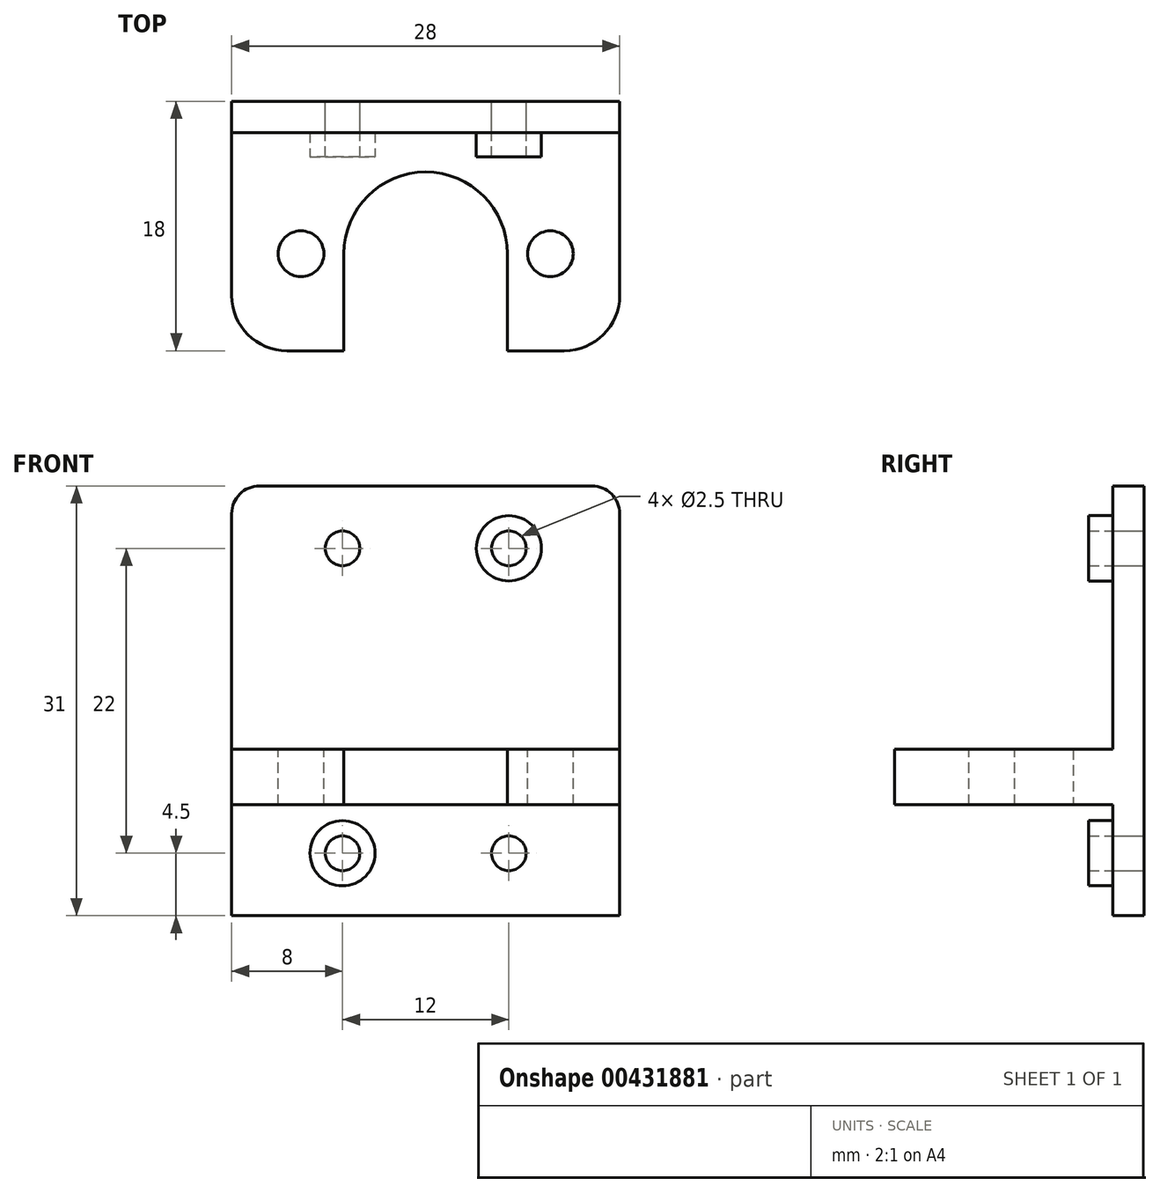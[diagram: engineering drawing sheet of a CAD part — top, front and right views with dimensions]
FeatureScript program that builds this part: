
annotation { "Feature Type Name" : "Feature", "Feature Type Description" : "" }
export const myFeature = defineFeature(function(context is Context, id is Id, definition is map)
    precondition{}
    {
        {
            var Q0;
            Q0=qCreatedBy(makeId("Front.planeOp"),FACE);
            var sketch = newSketch(context, id + "F0", { "sketchPlane" : qUnion([Q0])});
            skLineSegment(sketch, "E0.bottom", {"start": v(28, 31) * mm, "end": v(0, 31) * mm});
            skLineSegment(sketch, "E0.top", {"start": v(28, 0) * mm, "end": v(0, 0) * mm});
            skLineSegment(sketch, "E0.left", {"start": v(28, 31) * mm, "end": v(28, 0) * mm});
            skLineSegment(sketch, "E0.right", {"start": v(0, 31) * mm, "end": v(0, 0) * mm});
            skSolve(sketch);
        }
        {
            var Q0;
            Q0=makeQuery(id+"F0.imprint","IMPRINT",FACE,{"disambiguationData":[TD([[makeQuery(id+"F0.imprint","IMPRINT",EDGE,{"derivedFrom":sQuery(id+"F0.wireOp",EDGE,"E0.bottom")}),1.0]])]});
            extrude(context, id + "F1", {"entities" : qUnion([Q0]), "depth" : 4 * mm});
        }
        {
            var Q0;
            Q0=makeQuery(id+"F1.opExtrude","CAP_FACE",FACE,{"disambiguationData":[OSD([sQuery(id+"F0.wireOp",EDGE,"E0.bottom"),sQuery(id+"F0.wireOp",EDGE,"E0.top"),sQuery(id+"F0.wireOp",EDGE,"E0.left"),sQuery(id+"F0.wireOp",EDGE,"E0.right")])],"isStart":false});
            var sketch = newSketch(context, id + "F2", { "sketchPlane" : qUnion([Q0])});
            skLineSegment(sketch, "E1.bottom", {"start": v(0, 8) * mm, "end": v(28, 8) * mm});
            skLineSegment(sketch, "E1.top", {"start": v(0, 12) * mm, "end": v(28, 12) * mm});
            skLineSegment(sketch, "E1.left", {"start": v(0, 8) * mm, "end": v(0, 12) * mm});
            skLineSegment(sketch, "E1.right", {"start": v(28, 8) * mm, "end": v(28, 12) * mm});
            skLineSegment(sketch, "E2", {"start": v(0, 26.5) * mm, "end": v(28, 26.5) * mm, "construction": true});
            skLineSegment(sketch, "E3", {"start": v(0, 4.5) * mm, "end": v(28, 4.5) * mm, "construction": true});
            skLineSegment(sketch, "E4", {"start": v(20, 0) * mm, "end": v(20, 31) * mm, "construction": true});
            skLineSegment(sketch, "E5", {"start": v(8, 0) * mm, "end": v(8, 31) * mm, "construction": true});
            skPoint(sketch, "E6", {"position": v(8, 26.5) * mm});
            skPoint(sketch, "E7", {"position": v(20, 26.5) * mm});
            skPoint(sketch, "E8", {"position": v(20, 4.5) * mm});
            skPoint(sketch, "E9", {"position": v(8, 4.5) * mm});
            skCircle(sketch, "E10", {"center": v(8, 26.5) * mm, "radius": 2.35 * mm});
            skLineSegment(sketch, "E11", {"start": v(0, 15.5) * mm, "end": v(28, 15.5) * mm, "construction": true});
            skLineSegment(sketch, "E12", {"start": v(14, 31) * mm, "end": v(14, 0) * mm, "construction": true});
            skCircle(sketch, "E13.MirrorC", {"center": v(20, 26.5) * mm, "radius": 2.35 * mm});
            skCircle(sketch, "E14.MirrorC", {"center": v(8, 4.5) * mm, "radius": 2.35 * mm});
            skCircle(sketch, "E15.MirrorC", {"center": v(20, 4.5) * mm, "radius": 2.35 * mm});
            skSolve(sketch);
        }
        {
            var Q0;
            Q0=sQuery(id+"F2.wireOp",VERTEX,"E6");
            var Q1;
            Q1=sQuery(id+"F2.wireOp",VERTEX,"E7");
            var Q2;
            Q2=sQuery(id+"F2.wireOp",VERTEX,"E8");
            var Q3;
            Q3=sQuery(id+"F2.wireOp",VERTEX,"E9");
            var Q4;
            Q4=makeQuery(id+"F1.opExtrude","SWEPT_BODY",BODY,{"disambiguationData":[OSD([sQuery(id+"F0.wireOp",EDGE,"E0.bottom"),sQuery(id+"F0.wireOp",EDGE,"E0.top"),sQuery(id+"F0.wireOp",EDGE,"E0.left"),sQuery(id+"F0.wireOp",EDGE,"E0.right")])]});
            hole(context, id + "F3", {"style" : HoleStyle.SIMPLE, "endStyle" : HoleEndStyle.THROUGH, "holeDiameter" : 2.5 * mm, "isTappedThrough" : true, "tappedDepth" : 12 * mm, "tapClearance" : 3, "locations" : qUnion([Q0, Q1, Q2, Q3]), "scope" : qUnion([Q4]), "startStyle" : HoleStartStyle.PART});
        }
        {
            var Q0;
            Q0=makeQuery(id+"F2.imprint","IMPRINT",FACE,{"disambiguationData":[TD([[makeQuery(id+"F2.imprint","IMPRINT",EDGE,{"derivedFrom":sQuery(id+"F2.wireOp",EDGE,"E1.bottom")}),1.0]])]});
            extrude(context, id + "F4", {"entities" : qUnion([Q0]), "operationType" : NewBodyOperationType.ADD, "depth" : 14 * mm});
        }
        {
            var Q0;
            Q0=makeQuery(id+"F4.opExtrude","SWEPT_FACE",FACE,{"disambiguationData":[OSD([sQuery(id+"F2.wireOp",EDGE,"E1.bottom")])]});
            var sketch = newSketch(context, id + "F5", { "sketchPlane" : qUnion([Q0])});
            skLineSegment(sketch, "E16", {"start": v(0, 11) * mm, "end": v(28, 11) * mm, "construction": true});
            skLineSegment(sketch, "E17", {"start": v(14, 18) * mm, "end": v(14, 4) * mm, "construction": true});
            skCircle(sketch, "E18", {"center": v(14, 11) * mm, "radius": 5.9 * mm});
            skPoint(sketch, "E19", {"position": v(5, 11) * mm});
            skPoint(sketch, "E20", {"position": v(23, 11) * mm});
            skLineSegment(sketch, "E21", {"start": v(8.1, 11) * mm, "end": v(8.1, 18) * mm});
            skLineSegment(sketch, "E22", {"start": v(19.9, 11) * mm, "end": v(19.9, 18) * mm});
            skSolve(sketch);
        }
        {
            var Q0;
            {var subQ0=sQuery(id+"F5.wireOp",EDGE,"E21");Q0=makeQuery(id+"F5.imprint","IMPRINT",FACE,{"disambiguationData":[TD([[makeQuery(id+"F5.imprint","IMPRINT",EDGE,{"derivedFrom":subQ0}),-1.0]])]});}
            var Q1;
            {var subQ0=sQuery(id+"F5.wireOp",EDGE,"E18");var subQ1=makeQuery(id+"F5.imprint","INTERSECT",VERTEX,{"derivedFrom":[subQ0,sQuery(id+"F5.wireOp",EDGE,"E21")]});Q1=makeQuery(id+"F5.imprint","IMPRINT",FACE,{"disambiguationData":[TD([[makeQuery(id+"F5.imprint","IMPRINT",EDGE,{"disambiguationData":[TD([[subQ1,1.0]])],"derivedFrom":subQ0}),1.0]])]});}
            extrude(context, id + "F6", {"entities" : qUnion([Q0, Q1]), "operationType" : NewBodyOperationType.REMOVE, "oppositeDirection" : true, "depth" : 25 * mm});
        }
        {
            var Q0;
            Q0=sQuery(id+"F5.wireOp",VERTEX,"E19");
            var Q1;
            Q1=sQuery(id+"F5.wireOp",VERTEX,"E20");
            var Q2;
            Q2=makeQuery(id+"F1.opExtrude","SWEPT_BODY",BODY,{"disambiguationData":[OSD([sQuery(id+"F0.wireOp",EDGE,"E0.bottom"),sQuery(id+"F0.wireOp",EDGE,"E0.top"),sQuery(id+"F0.wireOp",EDGE,"E0.left"),sQuery(id+"F0.wireOp",EDGE,"E0.right")])]});
            hole(context, id + "F7", {"style" : HoleStyle.SIMPLE, "endStyle" : HoleEndStyle.THROUGH, "standardTappedOrClearance" : lookupTablePath({ "standard" : "ISO", "fit" : "Normal", "size" : "M3", "type" : "Clearance" }), "standardBlindInLast" : lookupTablePath({ "fit" : "Standard", "standard" : "ISO", "size" : "M3", "type" : "Clearance" }), "holeDiameter" : 3.3 * mm, "isTappedThrough" : true, "tappedDepth" : 12 * mm, "tapClearance" : 3, "locations" : qUnion([Q0, Q1]), "scope" : qUnion([Q2]), "startStyle" : HoleStartStyle.PART});
        }
        {
            var Q0;
            Q0=makeQuery(id+"F4.opExtrude","CAP_EDGE",EDGE,{"disambiguationData":[OSD([sQuery(id+"F2.wireOp",EDGE,"E1.right")])],"isStart":false});
            var Q1;
            Q1=makeQuery(id+"F6.boolean.opBoolean","COPY",EDGE,{"derivedFrom":makeQuery(id+"F6.opExtrude","SWEPT_EDGE",EDGE,{"disambiguationData":[OSD([sQuery(id+"F2.wireOp",EDGE,"E1.bottom"),sQuery(id+"F5.wireOp",EDGE,"E22")])]})});
            var Q2;
            Q2=makeQuery(id+"F6.boolean.opBoolean","COPY",EDGE,{"derivedFrom":makeQuery(id+"F6.opExtrude","SWEPT_EDGE",EDGE,{"disambiguationData":[OSD([sQuery(id+"F2.wireOp",EDGE,"E1.bottom"),sQuery(id+"F5.wireOp",EDGE,"E21")])]})});
            var Q3;
            Q3=makeQuery(id+"F4.opExtrude","CAP_EDGE",EDGE,{"disambiguationData":[OSD([sQuery(id+"F2.wireOp",EDGE,"E1.left")])],"isStart":false});
            fillet(context, id + "F8", {"entities" : qUnion([Q0, Q1, Q2, Q3]), "radius" : 4 * mm, "tangentPropagation" : true, "allowEdgeOverflow" : false});
        }
        {
            var Q0;
            Q0=makeQuery(id+"F1.opExtrude","SWEPT_EDGE",EDGE,{"disambiguationData":[OSD([sQuery(id+"F0.wireOp",EDGE,"E0.bottom"),sQuery(id+"F0.wireOp",EDGE,"E0.left")])]});
            var Q1;
            Q1=makeQuery(id+"F1.opExtrude","SWEPT_EDGE",EDGE,{"disambiguationData":[OSD([sQuery(id+"F0.wireOp",EDGE,"E0.bottom"),sQuery(id+"F0.wireOp",EDGE,"E0.right")])]});
            fillet(context, id + "F9", {"entities" : qUnion([Q0, Q1]), "radius" : 2 * mm, "tangentPropagation" : true, "allowEdgeOverflow" : false});
        }
        {
            var Q0;
            Q0=makeQuery(id+"F2.imprint","IMPRINT",FACE,{"disambiguationData":[TD([[makeQuery(id+"F2.imprint","IMPRINT",EDGE,{"derivedFrom":sQuery(id+"F2.wireOp",EDGE,"E10")}),1.0]])]});
            var Q1;
            Q1=makeQuery(id+"F2.imprint","IMPRINT",FACE,{"disambiguationData":[TD([[makeQuery(id+"F2.imprint","IMPRINT",EDGE,{"derivedFrom":sQuery(id+"F2.wireOp",EDGE,"E13.MirrorC")}),-1.0]])]});
            var Q2;
            Q2=makeQuery(id+"F2.imprint","IMPRINT",FACE,{"disambiguationData":[TD([[makeQuery(id+"F2.imprint","IMPRINT",EDGE,{"derivedFrom":sQuery(id+"F2.wireOp",EDGE,"E15.MirrorC")}),1.0]])]});
            var Q3;
            Q3=makeQuery(id+"F2.imprint","IMPRINT",FACE,{"disambiguationData":[TD([[makeQuery(id+"F2.imprint","IMPRINT",EDGE,{"derivedFrom":sQuery(id+"F2.wireOp",EDGE,"E14.MirrorC")}),-1.0]])]});
            extrude(context, id + "F10", {"entities" : qUnion([Q0, Q1, Q2, Q3]), "operationType" : NewBodyOperationType.REMOVE, "oppositeDirection" : true, "depth" : 1.75 * mm});
        }
    });
